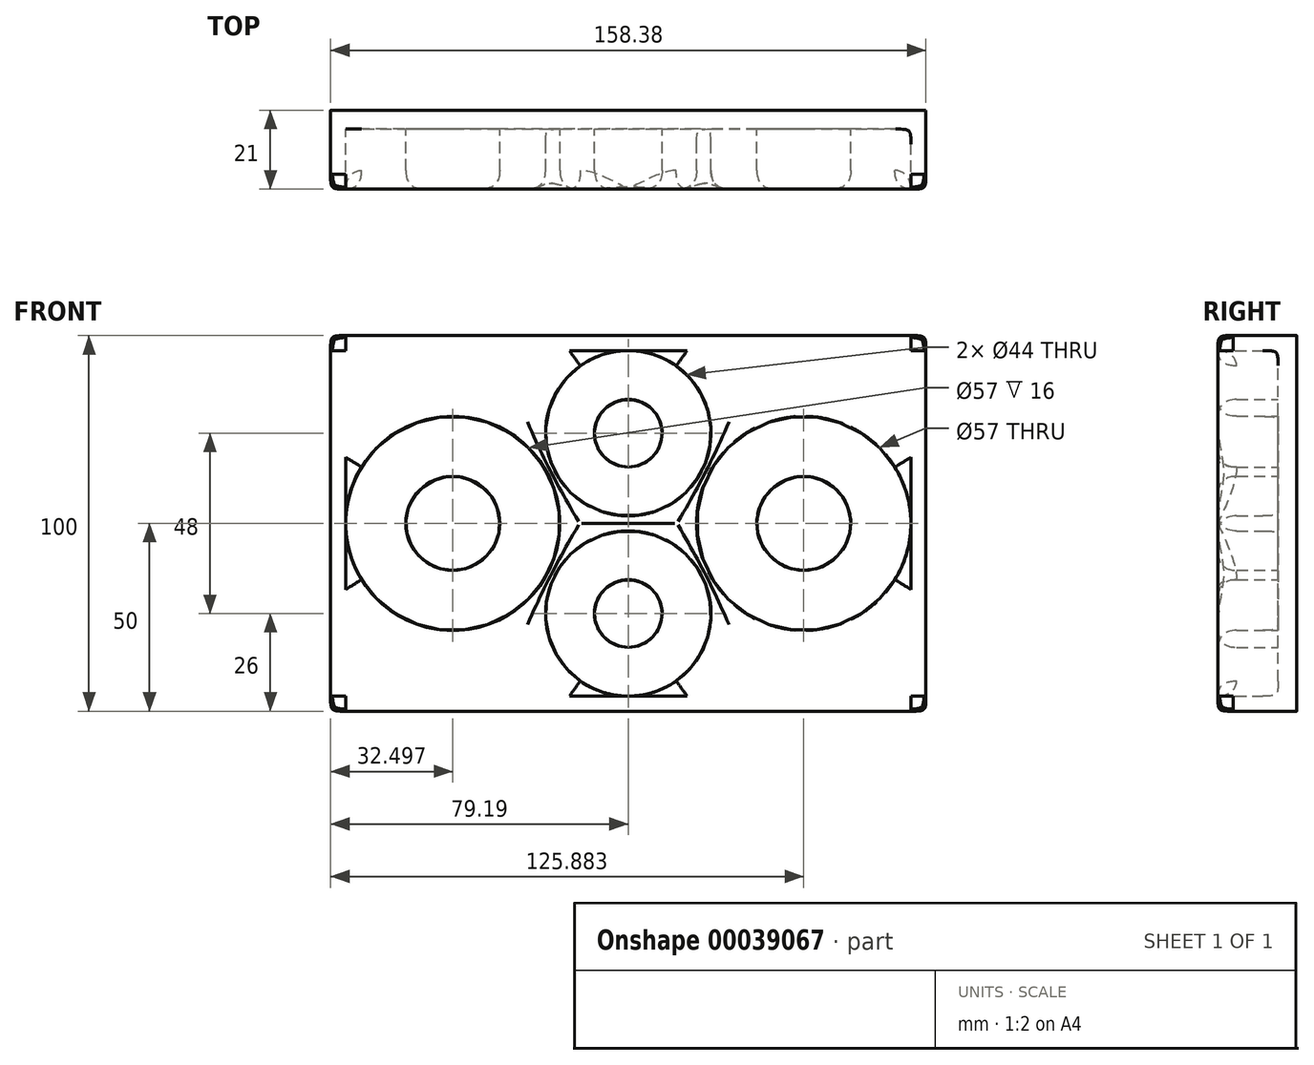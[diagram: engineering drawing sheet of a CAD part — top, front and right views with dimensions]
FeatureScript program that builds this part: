
annotation { "Feature Type Name" : "Feature", "Feature Type Description" : "" }
export const myFeature = defineFeature(function(context is Context, id is Id, definition is map)
    precondition{}
    {
        {
            var Q0;
            Q0=qCreatedBy(makeId("Front.planeOp"),FACE);
            var sketch = newSketch(context, id + "F0", { "sketchPlane" : qUnion([Q0])});
            skLineSegment(sketch, "E0.rect.bottom", {"start": v(79.2, -50) * mm, "end": v(-79.2, -50) * mm});
            skLineSegment(sketch, "E0.rect.top", {"start": v(79.2, 50) * mm, "end": v(-79.2, 50) * mm});
            skLineSegment(sketch, "E0.rect.left", {"start": v(79.2, -50) * mm, "end": v(79.2, 50) * mm});
            skLineSegment(sketch, "E0.rect.right", {"start": v(-79.2, -50) * mm, "end": v(-79.2, 50) * mm});
            skPoint(sketch, "E0.rect.middle", {"position": v(0, 0) * mm});
            skCircle(sketch, "E1", {"center": v(-46.7, 0) * mm, "radius": 28.5 * mm});
            skCircle(sketch, "E2", {"center": v(46.7, 0) * mm, "radius": 28.5 * mm});
            skLineSegment(sketch, "E3", {"start": v(-46.7, 0) * mm, "end": v(46.7, 0) * mm, "construction": true});
            skCircle(sketch, "E4", {"center": v(0, 24) * mm, "radius": 22 * mm});
            skCircle(sketch, "E5", {"center": v(0, -24) * mm, "radius": 22 * mm});
            skLineSegment(sketch, "E6", {"start": v(-21.35, 13.03) * mm, "end": v(-19.57, 13.94) * mm, "construction": true});
            skLineSegment(sketch, "E7", {"start": v(19.57, 13.94) * mm, "end": v(21.35, 13.03) * mm, "construction": true});
            skLineSegment(sketch, "E8", {"start": v(21.35, -13.03) * mm, "end": v(19.57, -13.94) * mm, "construction": true});
            skLineSegment(sketch, "E9", {"start": v(-19.57, -13.94) * mm, "end": v(-21.35, -13.03) * mm, "construction": true});
            skLineSegment(sketch, "E10", {"start": v(0, 2) * mm, "end": v(0, -2) * mm, "construction": true});
            skCircle(sketch, "E11", {"center": v(0, 24) * mm, "radius": 9 * mm});
            skCircle(sketch, "E12", {"center": v(0, -24) * mm, "radius": 9 * mm});
            skCircle(sketch, "E13", {"center": v(46.7, 0) * mm, "radius": 12.5 * mm});
            skCircle(sketch, "E14", {"center": v(-46.7, 0) * mm, "radius": 12.5 * mm});
            skSolve(sketch);
        }
        {
            var Q0;
            Q0=makeQuery(id+"F0.imprint","IMPRINT",FACE,{"disambiguationData":[TD([[makeQuery(id+"F0.imprint","IMPRINT",EDGE,{"derivedFrom":sQuery(id+"F0.wireOp",EDGE,"E14")}),1.0]])]});
            var Q1;
            Q1=makeQuery(id+"F0.imprint","IMPRINT",FACE,{"disambiguationData":[TD([[makeQuery(id+"F0.imprint","IMPRINT",EDGE,{"derivedFrom":sQuery(id+"F0.wireOp",EDGE,"E12")}),1.0]])]});
            var Q2;
            Q2=makeQuery(id+"F0.imprint","IMPRINT",FACE,{"disambiguationData":[TD([[makeQuery(id+"F0.imprint","IMPRINT",EDGE,{"derivedFrom":sQuery(id+"F0.wireOp",EDGE,"E11")}),1.0]])]});
            var Q3;
            Q3=makeQuery(id+"F0.imprint","IMPRINT",FACE,{"disambiguationData":[TD([[makeQuery(id+"F0.imprint","IMPRINT",EDGE,{"derivedFrom":sQuery(id+"F0.wireOp",EDGE,"E13")}),1.0]])]});
            var Q4;
            Q4=makeQuery(id+"F0.imprint","IMPRINT",FACE,{"disambiguationData":[TD([[makeQuery(id+"F0.imprint","IMPRINT",EDGE,{"derivedFrom":sQuery(id+"F0.wireOp",EDGE,"E2")}),1.0]])]});
            var Q5;
            Q5=makeQuery(id+"F0.imprint","IMPRINT",FACE,{"disambiguationData":[TD([[makeQuery(id+"F0.imprint","IMPRINT",EDGE,{"derivedFrom":sQuery(id+"F0.wireOp",EDGE,"E4")}),1.0]])]});
            var Q6;
            Q6=makeQuery(id+"F0.imprint","IMPRINT",FACE,{"disambiguationData":[TD([[makeQuery(id+"F0.imprint","IMPRINT",EDGE,{"derivedFrom":sQuery(id+"F0.wireOp",EDGE,"E5")}),1.0]])]});
            var Q7;
            Q7=makeQuery(id+"F0.imprint","IMPRINT",FACE,{"disambiguationData":[TD([[makeQuery(id+"F0.imprint","IMPRINT",EDGE,{"derivedFrom":sQuery(id+"F0.wireOp",EDGE,"E1")}),1.0]])]});
            var Q8;
            Q8=makeQuery(id+"F0.imprint","IMPRINT",FACE,{"disambiguationData":[TD([[makeQuery(id+"F0.imprint","IMPRINT",EDGE,{"derivedFrom":sQuery(id+"F0.wireOp",EDGE,"E0.rect.bottom")}),-1.0]])]});
            extrude(context, id + "F1", {"entities" : qUnion([Q0, Q1, Q2, Q3, Q4, Q5, Q6, Q7, Q8]), "oppositeDirection" : true, "depth" : 5 * mm});
        }
        {
            var Q0;
            Q0=makeQuery(id+"F0.imprint","IMPRINT",FACE,{"disambiguationData":[TD([[makeQuery(id+"F0.imprint","IMPRINT",EDGE,{"derivedFrom":sQuery(id+"F0.wireOp",EDGE,"E0.rect.bottom")}),-1.0]])]});
            var Q1;
            Q1=makeQuery(id+"F0.imprint","IMPRINT",FACE,{"disambiguationData":[TD([[makeQuery(id+"F0.imprint","IMPRINT",EDGE,{"derivedFrom":sQuery(id+"F0.wireOp",EDGE,"E14")}),1.0]])]});
            var Q2;
            Q2=makeQuery(id+"F0.imprint","IMPRINT",FACE,{"disambiguationData":[TD([[makeQuery(id+"F0.imprint","IMPRINT",EDGE,{"derivedFrom":sQuery(id+"F0.wireOp",EDGE,"E11")}),1.0]])]});
            var Q3;
            Q3=makeQuery(id+"F0.imprint","IMPRINT",FACE,{"disambiguationData":[TD([[makeQuery(id+"F0.imprint","IMPRINT",EDGE,{"derivedFrom":sQuery(id+"F0.wireOp",EDGE,"E13")}),1.0]])]});
            var Q4;
            Q4=makeQuery(id+"F0.imprint","IMPRINT",FACE,{"disambiguationData":[TD([[makeQuery(id+"F0.imprint","IMPRINT",EDGE,{"derivedFrom":sQuery(id+"F0.wireOp",EDGE,"E12")}),1.0]])]});
            extrude(context, id + "F2", {"entities" : qUnion([Q0, Q1, Q2, Q3, Q4]), "operationType" : NewBodyOperationType.ADD, "depth" : 16 * mm});
        }
        {
            var Q0;
            {var subQ0=sQuery(id+"F0.wireOp",EDGE,"E0.rect.bottom");var subQ1=sQuery(id+"F0.wireOp",EDGE,"E0.rect.right");Q0=makeQuery(id+"F2.boolean.opBoolean","MERGE",EDGE,{"derivedFrom":[makeQuery(id+"F1.opExtrude","SWEPT_EDGE",EDGE,{"disambiguationData":[OSD([subQ0,subQ1])]}),makeQuery(id+"F2.opExtrude","SWEPT_EDGE",EDGE,{"disambiguationData":[OSD([subQ0,subQ1])]})]});}
            var Q1;
            {var subQ0=sQuery(id+"F0.wireOp",EDGE,"E0.rect.bottom");var subQ1=sQuery(id+"F0.wireOp",EDGE,"E0.rect.left");Q1=makeQuery(id+"F2.boolean.opBoolean","MERGE",EDGE,{"derivedFrom":[makeQuery(id+"F1.opExtrude","SWEPT_EDGE",EDGE,{"disambiguationData":[OSD([subQ0,subQ1])]}),makeQuery(id+"F2.opExtrude","SWEPT_EDGE",EDGE,{"disambiguationData":[OSD([subQ0,subQ1])]})]});}
            var Q2;
            {var subQ0=sQuery(id+"F0.wireOp",EDGE,"E0.rect.top");var subQ1=sQuery(id+"F0.wireOp",EDGE,"E0.rect.right");Q2=makeQuery(id+"F2.boolean.opBoolean","MERGE",EDGE,{"derivedFrom":[makeQuery(id+"F1.opExtrude","SWEPT_EDGE",EDGE,{"disambiguationData":[OSD([subQ0,subQ1])]}),makeQuery(id+"F2.opExtrude","SWEPT_EDGE",EDGE,{"disambiguationData":[OSD([subQ0,subQ1])]})]});}
            var Q3;
            {var subQ0=sQuery(id+"F0.wireOp",EDGE,"E0.rect.top");var subQ1=sQuery(id+"F0.wireOp",EDGE,"E0.rect.left");Q3=makeQuery(id+"F2.boolean.opBoolean","MERGE",EDGE,{"derivedFrom":[makeQuery(id+"F1.opExtrude","SWEPT_EDGE",EDGE,{"disambiguationData":[OSD([subQ0,subQ1])]}),makeQuery(id+"F2.opExtrude","SWEPT_EDGE",EDGE,{"disambiguationData":[OSD([subQ0,subQ1])]})]});}
            var Q4;
            Q4=makeQuery(id+"F2.opExtrude","CAP_EDGE",EDGE,{"disambiguationData":[OSD([sQuery(id+"F0.wireOp",EDGE,"E0.rect.top")])],"isStart":false});
            var Q5;
            Q5=makeQuery(id+"F2.opExtrude","CAP_EDGE",EDGE,{"disambiguationData":[OSD([sQuery(id+"F0.wireOp",EDGE,"E0.rect.left")])],"isStart":false});
            var Q6;
            Q6=makeQuery(id+"F2.opExtrude","CAP_EDGE",EDGE,{"disambiguationData":[OSD([sQuery(id+"F0.wireOp",EDGE,"E0.rect.bottom")])],"isStart":false});
            var Q7;
            Q7=makeQuery(id+"F2.opExtrude","CAP_EDGE",EDGE,{"disambiguationData":[OSD([sQuery(id+"F0.wireOp",EDGE,"E0.rect.right")])],"isStart":false});
            var Q8;
            Q8=makeQuery(id+"F2.opExtrude","CAP_EDGE",EDGE,{"disambiguationData":[OSD([sQuery(id+"F0.wireOp",EDGE,"E2")])],"isStart":true});
            var Q9;
            Q9=makeQuery(id+"F2.opExtrude","CAP_EDGE",EDGE,{"disambiguationData":[OSD([sQuery(id+"F0.wireOp",EDGE,"E5")])],"isStart":true});
            var Q10;
            Q10=makeQuery(id+"F2.opExtrude","CAP_EDGE",EDGE,{"disambiguationData":[OSD([sQuery(id+"F0.wireOp",EDGE,"E4")])],"isStart":true});
            var Q11;
            Q11=makeQuery(id+"F2.opExtrude","CAP_EDGE",EDGE,{"disambiguationData":[OSD([sQuery(id+"F0.wireOp",EDGE,"E1")])],"isStart":true});
            fillet(context, id + "F3", {"entities" : qUnion([Q0, Q1, Q2, Q3, Q4, Q5, Q6, Q7, Q8, Q9, Q10, Q11]), "radius" : 4 * mm, "tangentPropagation" : true, "rho" : 0.74, "crossSection" : FilletCrossSection.CONIC, "allowEdgeOverflow" : false});
        }
        {
            var Q0;
            Q0=makeQuery(id+"F2.opExtrude","CAP_EDGE",EDGE,{"disambiguationData":[OSD([sQuery(id+"F0.wireOp",EDGE,"E2")])],"isStart":false});
            var Q1;
            Q1=makeQuery(id+"F2.opExtrude","CAP_EDGE",EDGE,{"disambiguationData":[OSD([sQuery(id+"F0.wireOp",EDGE,"E5")])],"isStart":false});
            var Q2;
            Q2=makeQuery(id+"F2.opExtrude","CAP_EDGE",EDGE,{"disambiguationData":[OSD([sQuery(id+"F0.wireOp",EDGE,"E4")])],"isStart":false});
            var Q3;
            Q3=makeQuery(id+"F2.opExtrude","CAP_EDGE",EDGE,{"disambiguationData":[OSD([sQuery(id+"F0.wireOp",EDGE,"E1")])],"isStart":false});
            var Q4;
            Q4=makeQuery(id+"F2.opExtrude","CAP_EDGE",EDGE,{"disambiguationData":[OSD([sQuery(id+"F0.wireOp",EDGE,"E14")])],"isStart":false});
            var Q5;
            Q5=makeQuery(id+"F2.opExtrude","CAP_EDGE",EDGE,{"disambiguationData":[OSD([sQuery(id+"F0.wireOp",EDGE,"E12")])],"isStart":false});
            var Q6;
            Q6=makeQuery(id+"F2.opExtrude","CAP_EDGE",EDGE,{"disambiguationData":[OSD([sQuery(id+"F0.wireOp",EDGE,"E13")])],"isStart":false});
            var Q7;
            Q7=makeQuery(id+"F2.opExtrude","CAP_EDGE",EDGE,{"disambiguationData":[OSD([sQuery(id+"F0.wireOp",EDGE,"E11")])],"isStart":false});
            fillet(context, id + "F4", {"entities" : qUnion([Q0, Q1, Q2, Q3, Q4, Q5, Q6, Q7]), "radius" : 5 * mm, "tangentPropagation" : true, "rho" : 0.5, "crossSection" : FilletCrossSection.CONIC, "allowEdgeOverflow" : false});
        }
    });
